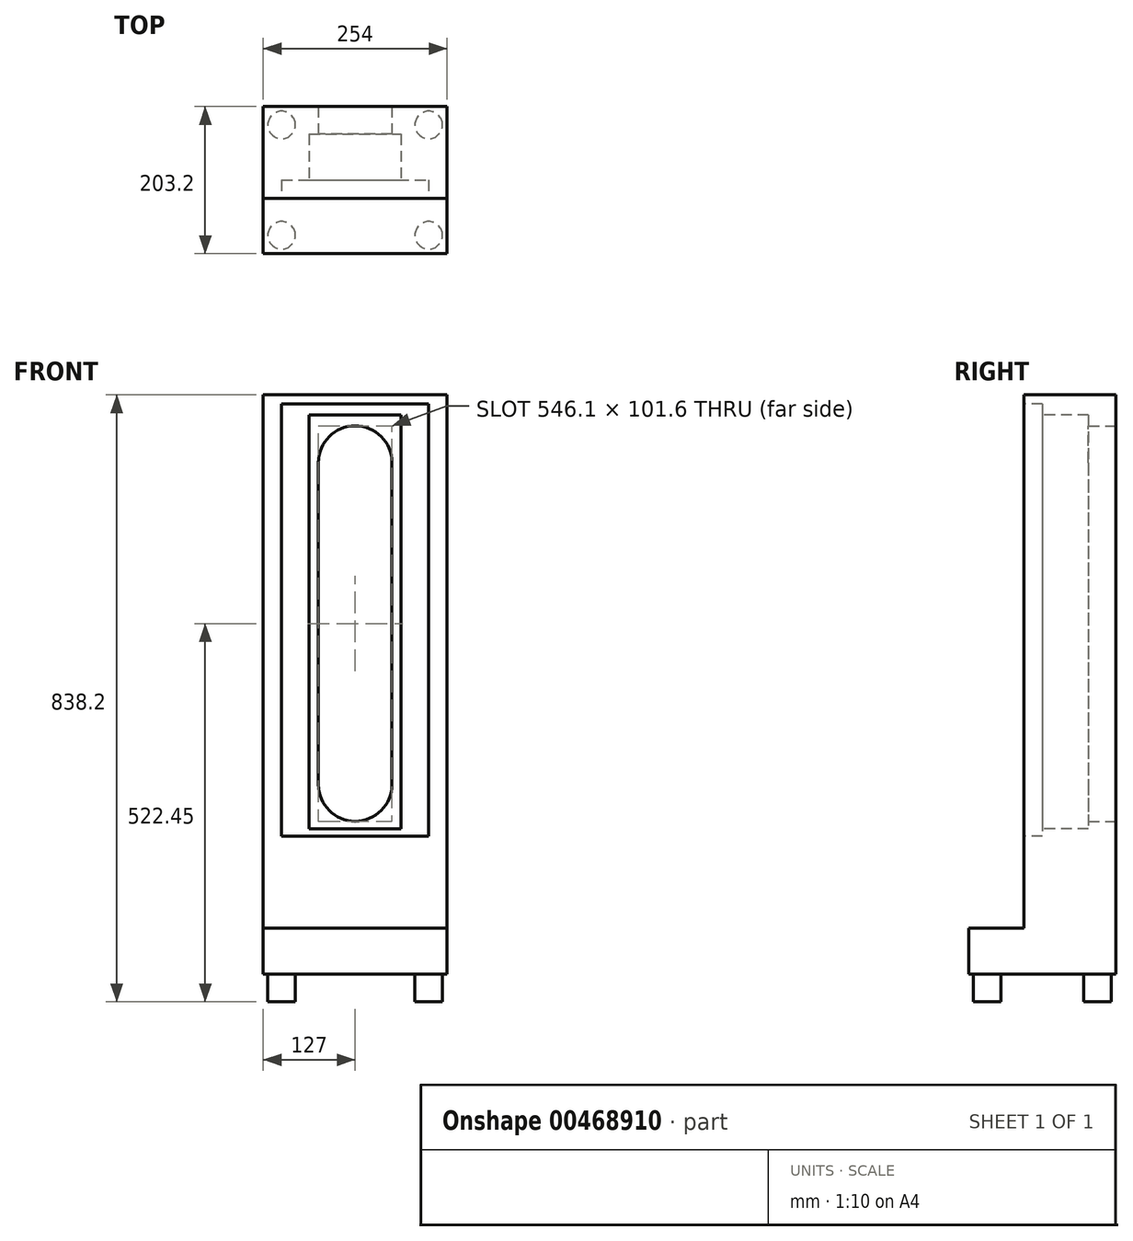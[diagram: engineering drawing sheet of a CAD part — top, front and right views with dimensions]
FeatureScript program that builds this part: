
annotation { "Feature Type Name" : "Feature", "Feature Type Description" : "" }
export const myFeature = defineFeature(function(context is Context, id is Id, definition is map)
    precondition{}
    {
        {
            var Q0;
            Q0=qCreatedBy(makeId("Front.planeOp"),FACE);
            var sketch = newSketch(context, id + "F0", { "sketchPlane" : qUnion([Q0])});
            skLineSegment(sketch, "E0.top", {"start": v(127, 609.6) * mm, "end": v(-127, 609.6) * mm});
            skLineSegment(sketch, "E0.left", {"start": v(127, -190.5) * mm, "end": v(127, 609.6) * mm});
            skLineSegment(sketch, "E0.right", {"start": v(-127, -190.5) * mm, "end": v(-127, 609.6) * mm});
            skPoint(sketch, "E1.middle", {"position": v(0, 0) * mm});
            skLineSegment(sketch, "E2", {"start": v(-127, -190.5) * mm, "end": v(127, -190.5) * mm});
            skPoint(sketch, "E3.orphan", {"position": v(-127, -609.6) * mm});
            skPoint(sketch, "E4.orphan", {"position": v(127, -609.6) * mm});
            skLineSegment(sketch, "E5.bottom", {"start": v(-101.6, 596.9) * mm, "end": v(101.6, 596.9) * mm});
            skLineSegment(sketch, "E5.top", {"start": v(-101.6, 0) * mm, "end": v(101.6, 0) * mm});
            skLineSegment(sketch, "E5.left", {"start": v(-101.6, 596.9) * mm, "end": v(-101.6, 0) * mm});
            skLineSegment(sketch, "E5.right", {"start": v(101.6, 596.9) * mm, "end": v(101.6, 0) * mm});
            skLineSegment(sketch, "E6.bottom", {"start": v(-63.5, 581.9) * mm, "end": v(63.5, 581.9) * mm});
            skLineSegment(sketch, "E6.top", {"start": v(-63.5, 10.4) * mm, "end": v(63.5, 10.4) * mm});
            skLineSegment(sketch, "E6.left", {"start": v(-63.5, 581.9) * mm, "end": v(-63.5, 10.4) * mm});
            skLineSegment(sketch, "E6.right", {"start": v(63.5, 581.9) * mm, "end": v(63.5, 10.4) * mm});
            skLineSegment(sketch, "E7.bottom", {"start": v(-50.8, 566.9) * mm, "end": v(50.8, 566.9) * mm});
            skLineSegment(sketch, "E7.top", {"start": v(-50.8, 20.8) * mm, "end": v(50.8, 20.8) * mm});
            skLineSegment(sketch, "E7.left", {"start": v(-50.8, 566.9) * mm, "end": v(-50.8, 20.8) * mm});
            skLineSegment(sketch, "E7.right", {"start": v(50.8, 566.9) * mm, "end": v(50.8, 20.8) * mm});
            skLineSegment(sketch, "E8", {"start": v(0, 870.13) * mm, "end": v(0, -870.13) * mm, "construction": true});
            skLineSegment(sketch, "E9.top", {"start": v(-127, -127) * mm, "end": v(127, -127) * mm});
            skLineSegment(sketch, "E9.left", {"start": v(-127, -190.5) * mm, "end": v(-127, -127) * mm});
            skLineSegment(sketch, "E9.right", {"start": v(127, -190.5) * mm, "end": v(127, -127) * mm});
            skSolve(sketch);
        }
        {
            var Q0;
            Q0=makeQuery(id+"F0.imprint","IMPRINT",FACE,{"disambiguationData":[TD([[makeQuery(id+"F0.imprint","IMPRINT",EDGE,{"derivedFrom":sQuery(id+"F0.wireOp",EDGE,"E0.top")}),1.0]])]});
            var Q1;
            Q1=makeQuery(id+"F0.imprint","IMPRINT",FACE,{"disambiguationData":[TD([[makeQuery(id+"F0.imprint","IMPRINT",EDGE,{"derivedFrom":sQuery(id+"F0.wireOp",EDGE,"E1.bottom")}),-1.0]])]});
            var Q2;
            Q2=makeQuery(id+"F0.imprint","IMPRINT",FACE,{"disambiguationData":[TD([[makeQuery(id+"F0.imprint","IMPRINT",EDGE,{"derivedFrom":sQuery(id+"F0.wireOp",EDGE,"l2cz76WN-11cX-8Qg5-Wc74-vKwfhGCtYGeO.bottom")}),-1.0]])]});
            var Q3;
            {var subQ0=sQuery(id+"F0.wireOp",EDGE,"dQK7Thth-TP6K-kbBQ-5Cwl-0GHNaYrmpQfn.left");var subQ1=sQuery(id+"F0.wireOp",EDGE,"E1.bottom");var subQ2=makeQuery(id+"F0.imprint","INTERSECT",VERTEX,{"derivedFrom":[subQ1,subQ0]});Q3=makeQuery(id+"F0.imprint","IMPRINT",FACE,{"disambiguationData":[TD([[makeQuery(id+"F0.imprint","IMPRINT",EDGE,{"disambiguationData":[TD([[subQ2,-1.0]])],"derivedFrom":subQ1}),1.0]])]});}
            var Q4;
            {var subQ5=sQuery(id+"F0.wireOp",EDGE,"huDVYpq4-8GHm-f6ov-cYvV-LWDsyoBmHsaB.top");Q4=makeQuery(id+"F0.imprint","IMPRINT",FACE,{"disambiguationData":[TD([[makeQuery(id+"F0.imprint","IMPRINT",EDGE,{"derivedFrom":subQ5}),1.0]])]});}
            var Q5;
            {var subQ5=sQuery(id+"F0.wireOp",EDGE,"dQK7Thth-TP6K-kbBQ-5Cwl-0GHNaYrmpQfn.bottom");Q5=makeQuery(id+"F0.imprint","IMPRINT",FACE,{"disambiguationData":[TD([[makeQuery(id+"F0.imprint","IMPRINT",EDGE,{"derivedFrom":subQ5}),-1.0]])]});}
            var Q6;
            {var subQ5=sQuery(id+"F0.wireOp",EDGE,"dQK7Thth-TP6K-kbBQ-5Cwl-0GHNaYrmpQfn.top");Q6=makeQuery(id+"F0.imprint","IMPRINT",FACE,{"disambiguationData":[TD([[makeQuery(id+"F0.imprint","IMPRINT",EDGE,{"derivedFrom":subQ5}),1.0]])]});}
            var Q7;
            {var subQ5=sQuery(id+"F0.wireOp",EDGE,"huDVYpq4-8GHm-f6ov-cYvV-LWDsyoBmHsaB.bottom");Q7=makeQuery(id+"F0.imprint","IMPRINT",FACE,{"disambiguationData":[TD([[makeQuery(id+"F0.imprint","IMPRINT",EDGE,{"derivedFrom":subQ5}),-1.0]])]});}
            var Q8;
            {var subQ0=sQuery(id+"F0.wireOp",EDGE,"dQK7Thth-TP6K-kbBQ-5Cwl-0GHNaYrmpQfn.left");var subQ1=sQuery(id+"F0.wireOp",EDGE,"E1.bottom");var subQ2=makeQuery(id+"F0.imprint","INTERSECT",VERTEX,{"derivedFrom":[subQ1,subQ0]});Q8=makeQuery(id+"F0.imprint","IMPRINT",FACE,{"disambiguationData":[TD([[makeQuery(id+"F0.imprint","IMPRINT",EDGE,{"disambiguationData":[TD([[subQ2,-1.0]])],"derivedFrom":subQ1}),-1.0]])]});}
            var Q9;
            Q9=makeQuery(id+"F0.imprint","IMPRINT",FACE,{"disambiguationData":[TD([[makeQuery(id+"F0.imprint","IMPRINT",EDGE,{"derivedFrom":sQuery(id+"F0.wireOp",EDGE,"E6.bottom")}),-1.0]])]});
            var Q10;
            Q10=makeQuery(id+"F0.imprint","IMPRINT",FACE,{"disambiguationData":[TD([[makeQuery(id+"F0.imprint","IMPRINT",EDGE,{"derivedFrom":sQuery(id+"F0.wireOp",EDGE,"E5.bottom")}),-1.0]])]});
            var Q11;
            Q11=makeQuery(id+"F0.imprint","IMPRINT",FACE,{"disambiguationData":[TD([[makeQuery(id+"F0.imprint","IMPRINT",EDGE,{"derivedFrom":sQuery(id+"F0.wireOp",EDGE,"E2")}),1.0]])]});
            extrude(context, id + "F1", {"entities" : qUnion([Q0, Q1, Q2, Q3, Q4, Q5, Q6, Q7, Q8, Q9, Q10, Q11]), "oppositeDirection" : true, "depth" : 127 * mm});
        }
        {
            var Q0;
            Q0=makeQuery(id+"F0.imprint","IMPRINT",FACE,{"disambiguationData":[TD([[makeQuery(id+"F0.imprint","IMPRINT",EDGE,{"derivedFrom":sQuery(id+"F0.wireOp",EDGE,"E5.bottom")}),-1.0]])]});
            extrude(context, id + "F2", {"entities" : qUnion([Q0]), "operationType" : NewBodyOperationType.REMOVE, "oppositeDirection" : true, "depth" : 25.4 * mm});
        }
        {
            var Q0;
            Q0=makeQuery(id+"F0.imprint","IMPRINT",FACE,{"disambiguationData":[TD([[makeQuery(id+"F0.imprint","IMPRINT",EDGE,{"derivedFrom":sQuery(id+"F0.wireOp",EDGE,"E6.bottom")}),-1.0]])]});
            extrude(context, id + "F3", {"entities" : qUnion([Q0]), "operationType" : NewBodyOperationType.REMOVE, "oppositeDirection" : true, "depth" : 88.9 * mm});
        }
        {
            var Q0;
            Q0=makeQuery(id+"F1.opExtrude","SWEPT_EDGE",EDGE,{"disambiguationData":[OSD([sQuery(id+"F0.wireOp",EDGE,"E7.bottom"),sQuery(id+"F0.wireOp",EDGE,"E7.right")])]});
            var Q1;
            Q1=makeQuery(id+"F1.opExtrude","SWEPT_EDGE",EDGE,{"disambiguationData":[OSD([sQuery(id+"F0.wireOp",EDGE,"E7.bottom"),sQuery(id+"F0.wireOp",EDGE,"E7.left")])]});
            var Q2;
            Q2=makeQuery(id+"F1.opExtrude","SWEPT_EDGE",EDGE,{"disambiguationData":[OSD([sQuery(id+"F0.wireOp",EDGE,"E7.top"),sQuery(id+"F0.wireOp",EDGE,"E7.left")])]});
            var Q3;
            Q3=makeQuery(id+"F1.opExtrude","SWEPT_EDGE",EDGE,{"disambiguationData":[OSD([sQuery(id+"F0.wireOp",EDGE,"E7.top"),sQuery(id+"F0.wireOp",EDGE,"E7.right")])]});
            fillet(context, id + "F4", {"entities" : qUnion([Q0, Q1, Q2, Q3]), "radius" : 50.8 * mm, "tangentPropagation" : true, "allowEdgeOverflow" : false});
        }
        {
            var Q0;
            Q0=makeQuery(id+"F0.imprint","IMPRINT",FACE,{"disambiguationData":[TD([[makeQuery(id+"F0.imprint","IMPRINT",EDGE,{"derivedFrom":sQuery(id+"F0.wireOp",EDGE,"E2")}),1.0]])]});
            extrude(context, id + "F5", {"entities" : qUnion([Q0]), "operationType" : NewBodyOperationType.ADD, "depth" : 76.2 * mm});
        }
        {
            var Q0;
            {var subQ0=sQuery(id+"F0.wireOp",EDGE,"E2");Q0=makeQuery(id+"F5.boolean.opBoolean","MERGE",FACE,{"derivedFrom":[makeQuery(id+"F1.opExtrude","SWEPT_FACE",FACE,{"disambiguationData":[OSD([subQ0])]}),makeQuery(id+"F5.opExtrude","SWEPT_FACE",FACE,{"disambiguationData":[OSD([subQ0])]})]});}
            var sketch = newSketch(context, id + "F6", { "sketchPlane" : qUnion([Q0])});
            skCircle(sketch, "E10", {"center": v(-101.6, 50.8) * mm, "radius": 19.05 * mm});
            skCircle(sketch, "E11", {"center": v(101.6, 50.8) * mm, "radius": 19.05 * mm});
            skCircle(sketch, "E12", {"center": v(-101.6, -101.6) * mm, "radius": 19.05 * mm});
            skCircle(sketch, "E13", {"center": v(101.6, -101.6) * mm, "radius": 19.05 * mm});
            skSolve(sketch);
        }
        {
            var Q0;
            Q0 = qSketchRegion(id + "F6", true);
            extrude(context, id + "F7", {"entities" : qUnion([Q0]), "operationType" : NewBodyOperationType.ADD, "depth" : 38.1 * mm});
        }
    });
